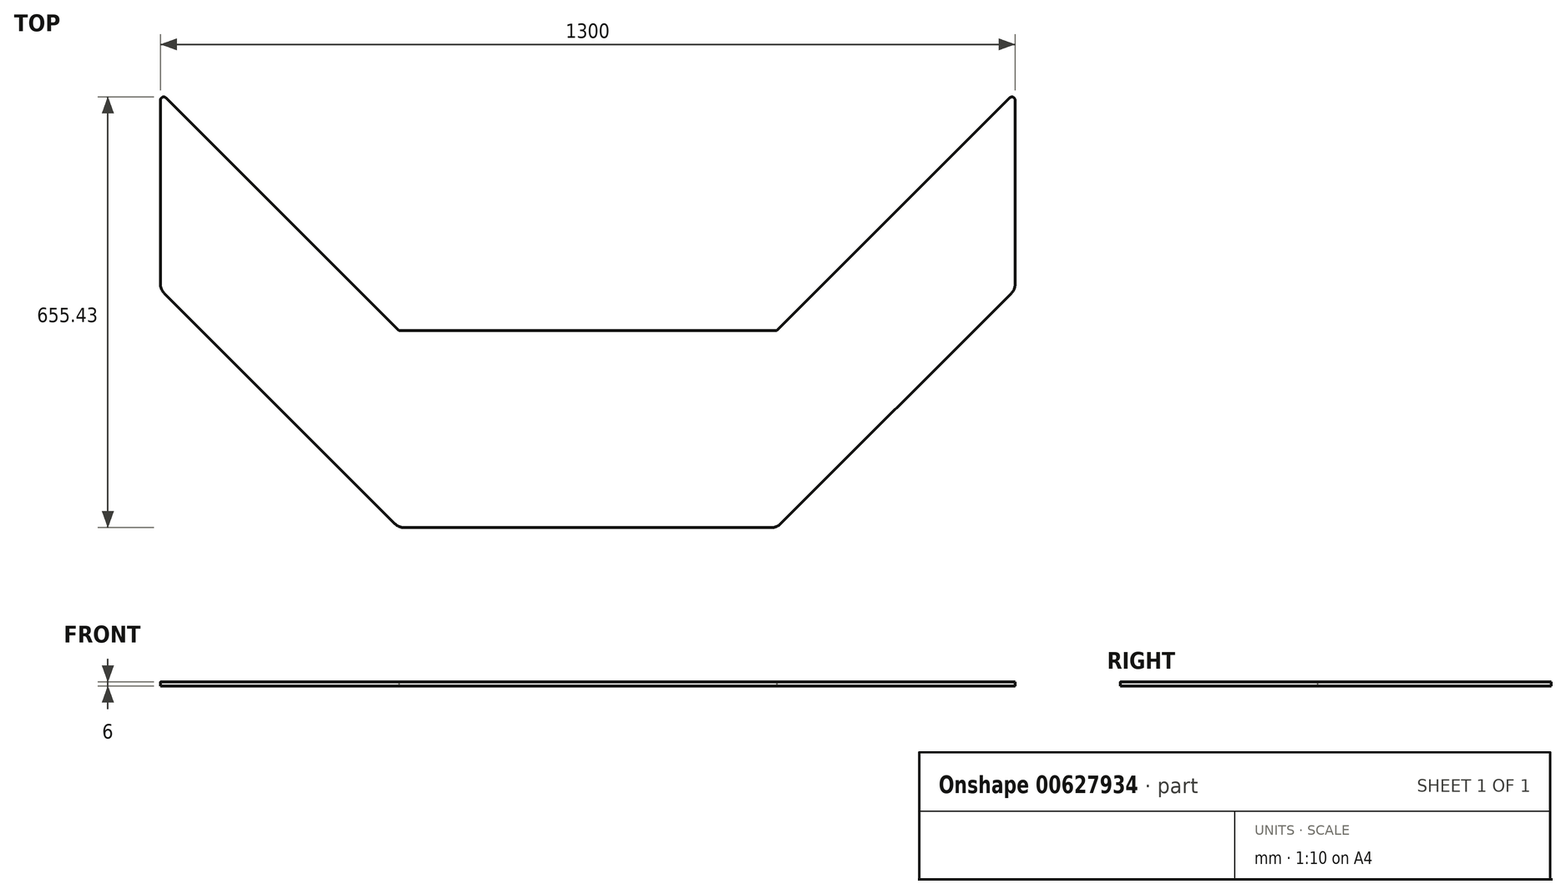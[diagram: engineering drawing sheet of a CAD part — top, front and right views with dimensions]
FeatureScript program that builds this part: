
annotation { "Feature Type Name" : "Feature", "Feature Type Description" : "" }
export const myFeature = defineFeature(function(context is Context, id is Id, definition is map)
    precondition{}
    {
        {
            var Q0;
            Q0=qCreatedBy(makeId("Top.planeOp"),FACE);
            var sketch = newSketch(context, id + "F0", { "sketchPlane" : qUnion([Q0])});
            skLineSegment(sketch, "E0", {"start": v(-287.5, 150) * mm, "end": v(287.5, 150) * mm});
            skLineSegment(sketch, "E1", {"start": v(287.5, 150) * mm, "end": v(641.46, 503.96) * mm});
            skLineSegment(sketch, "E2", {"start": v(650, 500.43) * mm, "end": v(650, 220.78) * mm});
            skLineSegment(sketch, "E3", {"start": v(279.22, -150) * mm, "end": v(-279.22, -150) * mm});
            skLineSegment(sketch, "E4", {"start": v(-650, 220.78) * mm, "end": v(-650, 500.43) * mm});
            skLineSegment(sketch, "E5", {"start": v(-641.46, 503.96) * mm, "end": v(-287.5, 150) * mm});
            skLineSegment(sketch, "E6", {"start": v(293.36, -144.14) * mm, "end": v(644.14, 206.64) * mm});
            skPoint(sketch, "E7.orphan", {"position": v(650, -150) * mm});
            skLineSegment(sketch, "E8", {"start": v(-644.14, 206.64) * mm, "end": v(-293.36, -144.14) * mm});
            skPoint(sketch, "E9.orphan", {"position": v(-650, -150) * mm});
            skLineSegment(sketch, "E10", {"start": v(-287.5, 150) * mm, "end": v(-287.5, -150) * mm, "construction": true});
            skLineSegment(sketch, "E11", {"start": v(287.5, 150) * mm, "end": v(287.5, -150) * mm, "construction": true});
            skPoint(sketch, "E12.visualSharp", {"position": v(-650, 512.5) * mm});
            skArc(sketch, "E12.filletArc", {"start": v(-641.46, 503.96) * mm, "mid": v(-646.91, 505.05) * mm, "end": v(-650, 500.43) * mm});
            skPoint(sketch, "E13.visualSharp", {"position": v(-650, 212.5) * mm});
            skArc(sketch, "E13.filletArc", {"start": v(-650, 220.78) * mm, "mid": v(-648.48, 213.13) * mm, "end": v(-644.14, 206.64) * mm});
            skPoint(sketch, "E14.visualSharp", {"position": v(-287.5, -150) * mm});
            skArc(sketch, "E14.filletArc", {"start": v(-293.36, -144.14) * mm, "mid": v(-286.87, -148.48) * mm, "end": v(-279.22, -150) * mm});
            skPoint(sketch, "E15.visualSharp", {"position": v(287.5, -150) * mm});
            skArc(sketch, "E15.filletArc", {"start": v(279.22, -150) * mm, "mid": v(286.87, -148.48) * mm, "end": v(293.36, -144.14) * mm});
            skPoint(sketch, "E16.visualSharp", {"position": v(650, 212.5) * mm});
            skArc(sketch, "E16.filletArc", {"start": v(644.14, 206.64) * mm, "mid": v(648.48, 213.13) * mm, "end": v(650, 220.78) * mm});
            skPoint(sketch, "E17.visualSharp", {"position": v(287.5, 150) * mm});
            skPoint(sketch, "E18.visualSharp", {"position": v(650, 512.5) * mm});
            skArc(sketch, "E18.filletArc", {"start": v(650, 500.43) * mm, "mid": v(646.91, 505.05) * mm, "end": v(641.46, 503.96) * mm});
            skSolve(sketch);
        }
        {
            var Q0;
            Q0=qSketchRegion(id+"F0",true);
            extrude(context, id + "F1", {"entities" : qUnion([Q0]), "depth" : 6 * mm, "offsetDistance" : 25 * mm});
        }
    });
